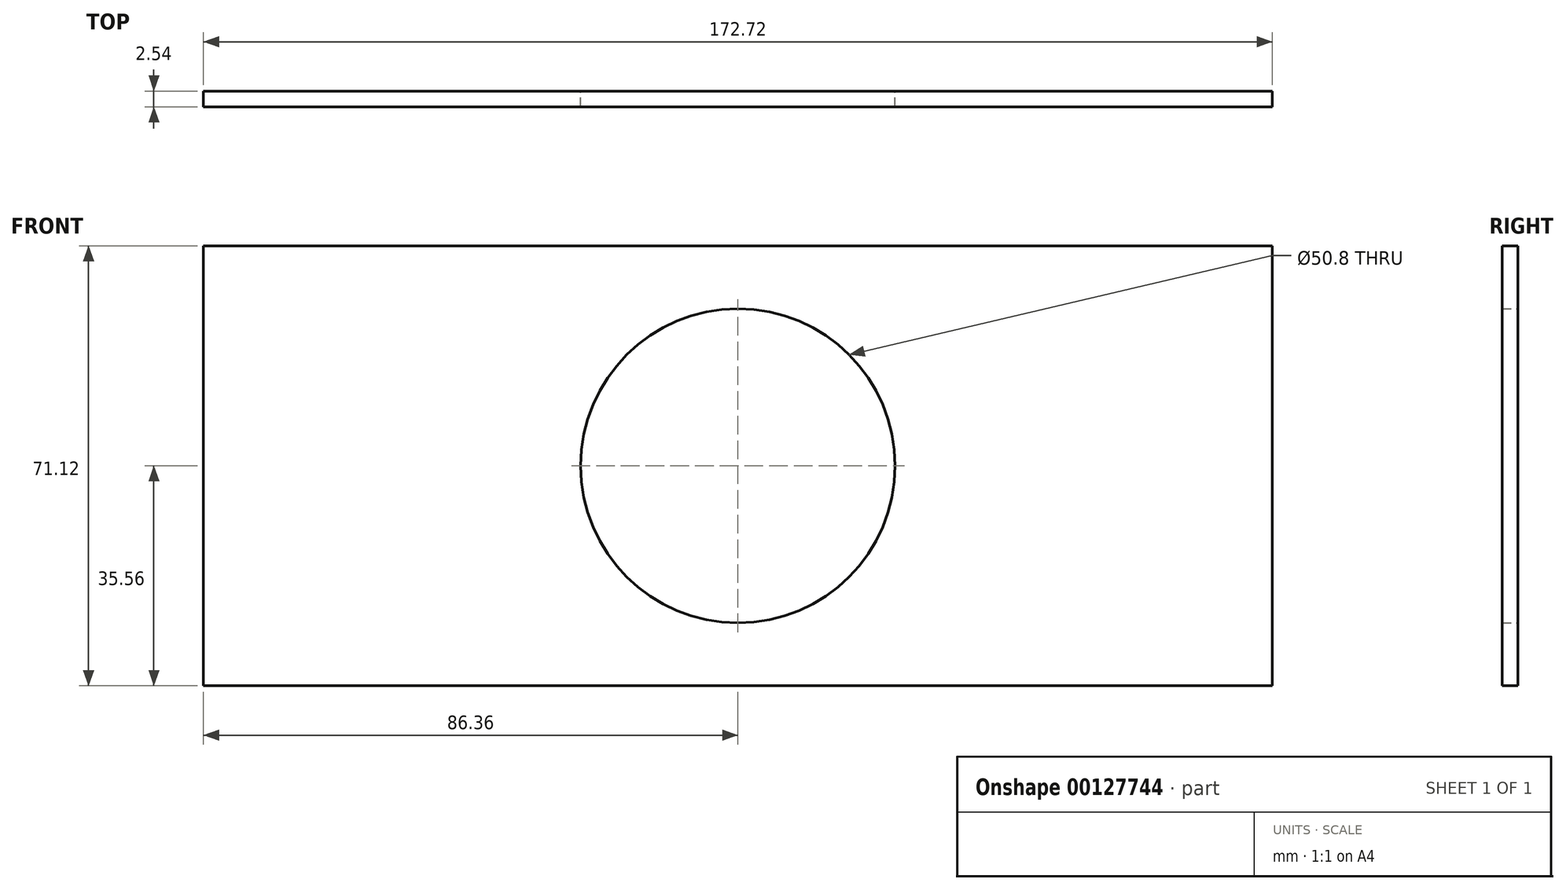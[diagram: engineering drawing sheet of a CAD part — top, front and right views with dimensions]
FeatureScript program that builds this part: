
annotation { "Feature Type Name" : "Feature", "Feature Type Description" : "" }
export const myFeature = defineFeature(function(context is Context, id is Id, definition is map)
    precondition{}
    {
        {
            var Q0;
            Q0=qCreatedBy(makeId("Front.planeOp"),FACE);
            var sketch = newSketch(context, id + "F0", { "sketchPlane" : qUnion([Q0])});
            skLineSegment(sketch, "E0.bottom", {"start": v(-86.36, 35.56) * mm, "end": v(86.36, 35.56) * mm});
            skLineSegment(sketch, "E0.top", {"start": v(-86.36, -35.56) * mm, "end": v(86.36, -35.56) * mm});
            skLineSegment(sketch, "E0.left", {"start": v(-86.36, 35.56) * mm, "end": v(-86.36, -35.56) * mm});
            skLineSegment(sketch, "E0.right", {"start": v(86.36, 35.56) * mm, "end": v(86.36, -35.56) * mm});
            skPoint(sketch, "E0.middle", {"position": v(0, 0) * mm});
            skCircle(sketch, "E1", {"center": v(0, 0) * mm, "radius": 25.4 * mm});
            skSolve(sketch);
        }
        {
            var Q0;
            Q0=makeQuery(id+"F0.imprint","IMPRINT",FACE,{"disambiguationData":[TD([[makeQuery(id+"F0.imprint","IMPRINT",EDGE,{"derivedFrom":sQuery(id+"F0.wireOp",EDGE,"E0.bottom")}),-1.0]])]});
            extrude(context, id + "F1", {"entities" : qUnion([Q0]), "depth" : 2.54 * mm});
        }
    });
